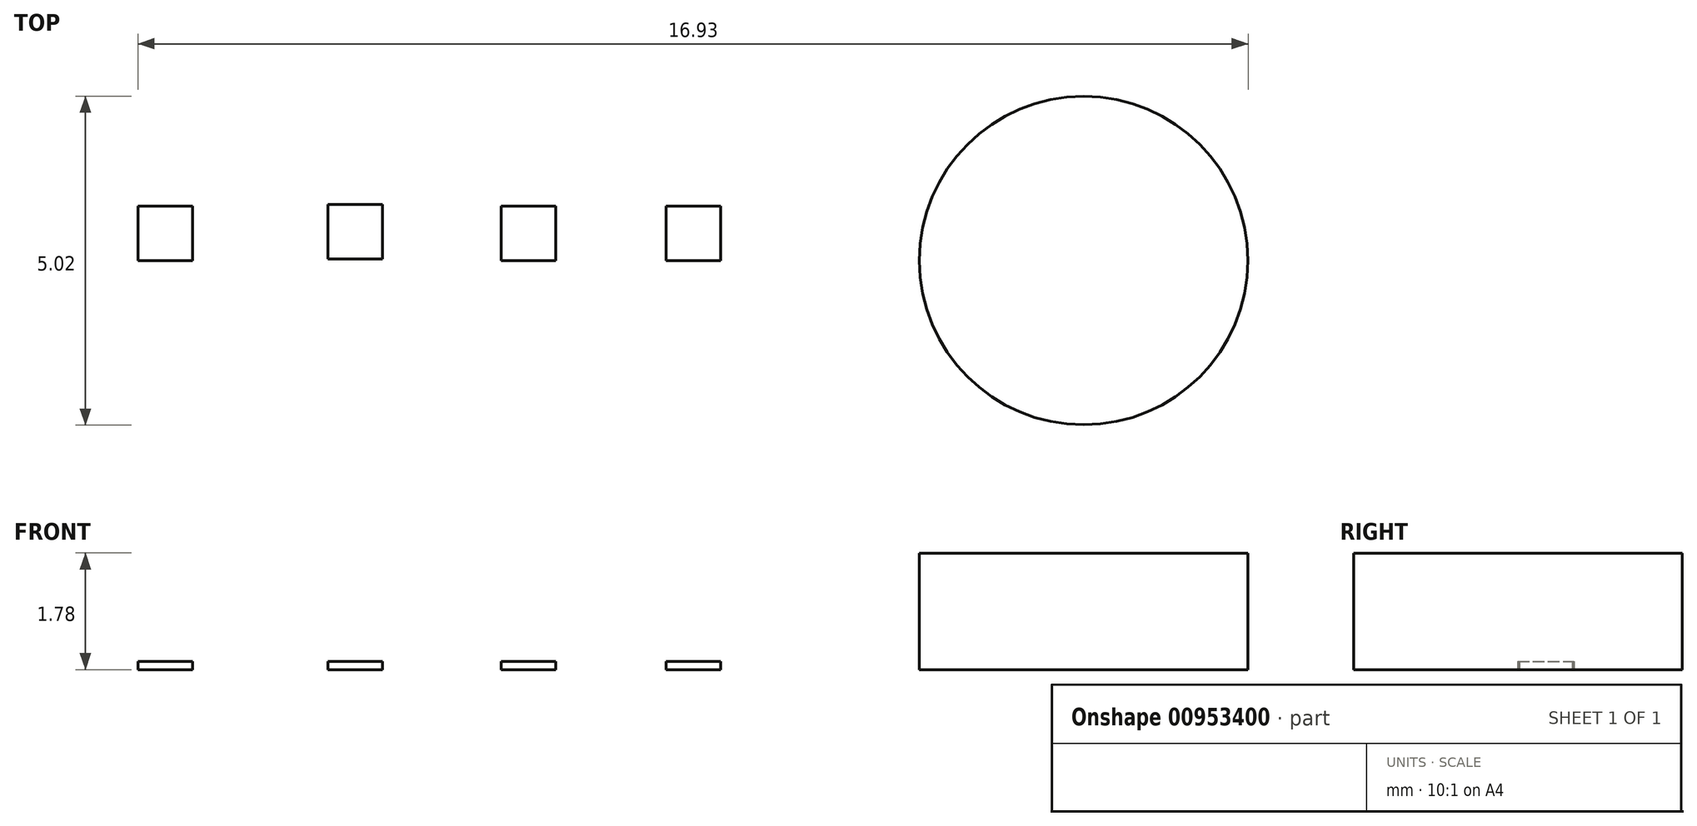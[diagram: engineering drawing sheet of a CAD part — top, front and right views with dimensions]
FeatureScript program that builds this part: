
annotation { "Feature Type Name" : "Feature", "Feature Type Description" : "" }
export const myFeature = defineFeature(function(context is Context, id is Id, definition is map)
    precondition{}
    {
        {
            var Q0;
            Q0=qCreatedBy(makeId("Top.planeOp"),FACE);
            var sketch = newSketch(context, id + "F0", { "sketchPlane" : qUnion([Q0])});
            skCircle(sketch, "E0", {"center": v(0, 0) * mm, "radius": 2.5 * mm});
            skSolve(sketch);
        }
        {
            var Q0;
            Q0=qSketchRegion(id+"F0",true);
            extrude(context, id + "F1", {"entities" : qUnion([Q0]), "depth" : 1.78 * mm, "offsetDistance" : 25.4 * mm});
        }
        {
            var Q0;
            Q0=qCreatedBy(makeId("Top.planeOp"),FACE);
            var sketch = newSketch(context, id + "F2", { "sketchPlane" : qUnion([Q0])});
            skLineSegment(sketch, "E1.bottom", {"start": v(-5.54, 0) * mm, "end": v(-6.37, 0) * mm});
            skLineSegment(sketch, "E1.top", {"start": v(-5.54, 0.83) * mm, "end": v(-6.37, 0.83) * mm});
            skLineSegment(sketch, "E1.left", {"start": v(-5.54, 0) * mm, "end": v(-5.54, 0.83) * mm});
            skLineSegment(sketch, "E1.right", {"start": v(-6.37, 0) * mm, "end": v(-6.37, 0.83) * mm});
            skSolve(sketch);
        }
        {
            var Q0;
            Q0=qSketchRegion(id+"F2",true);
            extrude(context, id + "F3", {"entities" : qUnion([Q0]), "depth" : 0.13 * mm, "offsetDistance" : 25.4 * mm});
        }
        {
            var Q0;
            Q0=makeQuery(id+"F3.opExtrude","SWEPT_BODY",BODY,{"disambiguationData":[OSD([sQuery(id+"F2.wireOp",EDGE,"E1.bottom"),sQuery(id+"F2.wireOp",EDGE,"E1.top"),sQuery(id+"F2.wireOp",EDGE,"E1.left"),sQuery(id+"F2.wireOp",EDGE,"E1.right")])]});
            transform(context, id + "F4", {"entities" : qUnion([Q0]), "transformType" : TransformType.TRANSLATION_3D, "dx" : -2.5 * mm, "dy" : 0 * mm, "dz" : 0 * mm, "makeCopy" : true});
        }
        {
            var Q0;
            Q0=makeQuery(id+"F3.opExtrude","SWEPT_BODY",BODY,{"disambiguationData":[OSD([sQuery(id+"F2.wireOp",EDGE,"E1.bottom"),sQuery(id+"F2.wireOp",EDGE,"E1.top"),sQuery(id+"F2.wireOp",EDGE,"E1.left"),sQuery(id+"F2.wireOp",EDGE,"E1.right")])]});
            transform(context, id + "F5", {"entities" : qUnion([Q0]), "transformType" : TransformType.TRANSLATION_3D, "dx" : -5.16 * mm, "dy" : 0.03 * mm, "dz" : 0 * mm, "makeCopy" : true});
        }
        {
            var Q0;
            Q0=makeQuery(id+"F3.opExtrude","SWEPT_BODY",BODY,{"disambiguationData":[OSD([sQuery(id+"F2.wireOp",EDGE,"E1.bottom"),sQuery(id+"F2.wireOp",EDGE,"E1.top"),sQuery(id+"F2.wireOp",EDGE,"E1.left"),sQuery(id+"F2.wireOp",EDGE,"E1.right")])]});
            transform(context, id + "F6", {"entities" : qUnion([Q0]), "transformType" : TransformType.TRANSLATION_3D, "dx" : -8.05 * mm, "dy" : 0 * mm, "dz" : 0 * mm, "makeCopy" : true});
        }
    });
